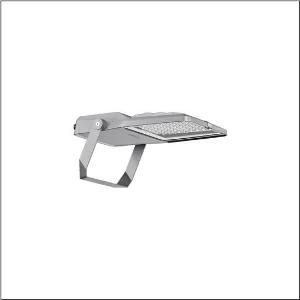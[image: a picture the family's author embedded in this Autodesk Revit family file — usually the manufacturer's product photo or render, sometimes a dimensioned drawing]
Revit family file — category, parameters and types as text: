
# Revit family: floodlight_fl_21_iq_mini___pl61_5xa7772b3c1a_b78d
name_source: partatom
category: Lighting Fixtures
units: mm (PartAtom-declared; Revit-internal decimal feet)

## family parameters
Cut with Voids When Loaded = No
Host = Face
Light Source = No
Part Type = Normal
Room Calculation Point = No
Round Connector Dimension = Use Diameter
Shared = No

## types (1)
- --- (1 x LED, 5270 lm, 45.5 W, 3000K)
    Apparent Load = 46 VA
    CIE Flux Codes = 33 65 98 100 100
    Color Rendering = 80
    Color Temperature = 3000K
    Default Elevation = 1800 mm
    Description = Floodlight FL 21 iQ mini, floodlight, primary light control with lens, of PMMA, primary optical cover: protective disc, of toughened safety glass, transparent, light distribution: PL61, light emission: direct distribution, installation type: surface-mounted, lamps: LED, High Power LED, rated values: 5.270lm | 45,5W | 115,8lm/W (begin service life); end service life: 5.270lm | 48W; at 50% lumin. flux: 2.635lm | 21,4W | 123,1lm/W, colour temperature: 3000K, colour rendering: CRI > 80, light colour: 830, light setting 1 begin service life: 100% | 5.270lm | 45,5W | 115,8lm/W | 3.000K, light setting 1 end service life: 48W, further light settings possible, control: Street-Remote, Auto-Match, Temp-Guard, Night-Set, Smart-Wire, Desk-Remote (wireless, voltage-free reading and setting of iQ features in the workshop via application-optimized NFC function/RFID function), optimised constant luminous flux control (CLO 2.0), pre-setting: linear dimming characteristic, with terminal, 6-pole, mains connection: 220..240V, AC, 50/60Hz, luminaire housing, of diecast aluminium, powder-coated, SITECO metallic grey (DB 702S), corrosivity category C5 mid according to DIN EN ISO 12944suitable for swimming poolschlorine-resistant, sealing non-destructively replaceable, mounting bracket, of steel, galvanised, powder-coated, SITECO metallic grey (DB 702S), protection rating (complete): IP66, insulation class (complete): insulation class II (safety insulation), certification: CE, ENEC, VDE, protection symbol: D, impact resistance: IK08, permissible operating ambient temperature: -40..+40°C, permissible operating ambient temperature for outdoor applications: -40..+50°C, standard: DIN EN 12944, LABS conformity tested according to VDMA 24364:2018-05, packaging unit: 1 piece

Light Distribution: PL61
    Height = 70 mm
    Lamp = 1 x LED
    Lamp Light Flux = 5270 lm
    Lamp Power = 45.5 W
    Lamp count = 1
    Length = 485 mm
    Luminous efficacy = 116 lm/W
    Manufacturer = Siteco
    ModVariant = No
    Model = 5XA7772B3C1A
    Mounting Place = Pole
    Mounting Type = Pole annexe
    Number of Poles = 1
    OnlyDefault = Yes
    Power Factor = 1
    Product Name = Floodlight FL 21 iQ mini | PL61
    Product group = floodlight | pylon annexe
    ProductGroupID = 6201
    Protection Class = Protection class II
    Protection Degree = IP 66
    RLX_Detail_Level = 1
    RLX_Emergency_Light_Flux = 0 lm
    RLX_Emergency_Type = 0
    RLX_Emergency_Type_DB = No
    RlxData = <blob elided: 96441 chars, md5=f884261c>
    Socket = socket
    Standby Power = 0 W
    System Light Flux = 5270 lm
    System Power = 46 W
    Type Comments = factory setting: luminous flux: 100 % | dim-lin: 254 | 463 mA
    Type Image = l_1006845.jpg
    URL = http://relux.com
    VarID = @adj_174589
    Voltage = 0 V
    Weight = 0.00 kg
    Width = 337 mm

## geometry (parser evidence)
native form markers: Blend x4, Sweep x13
no freeform markers — native parametric forms only
